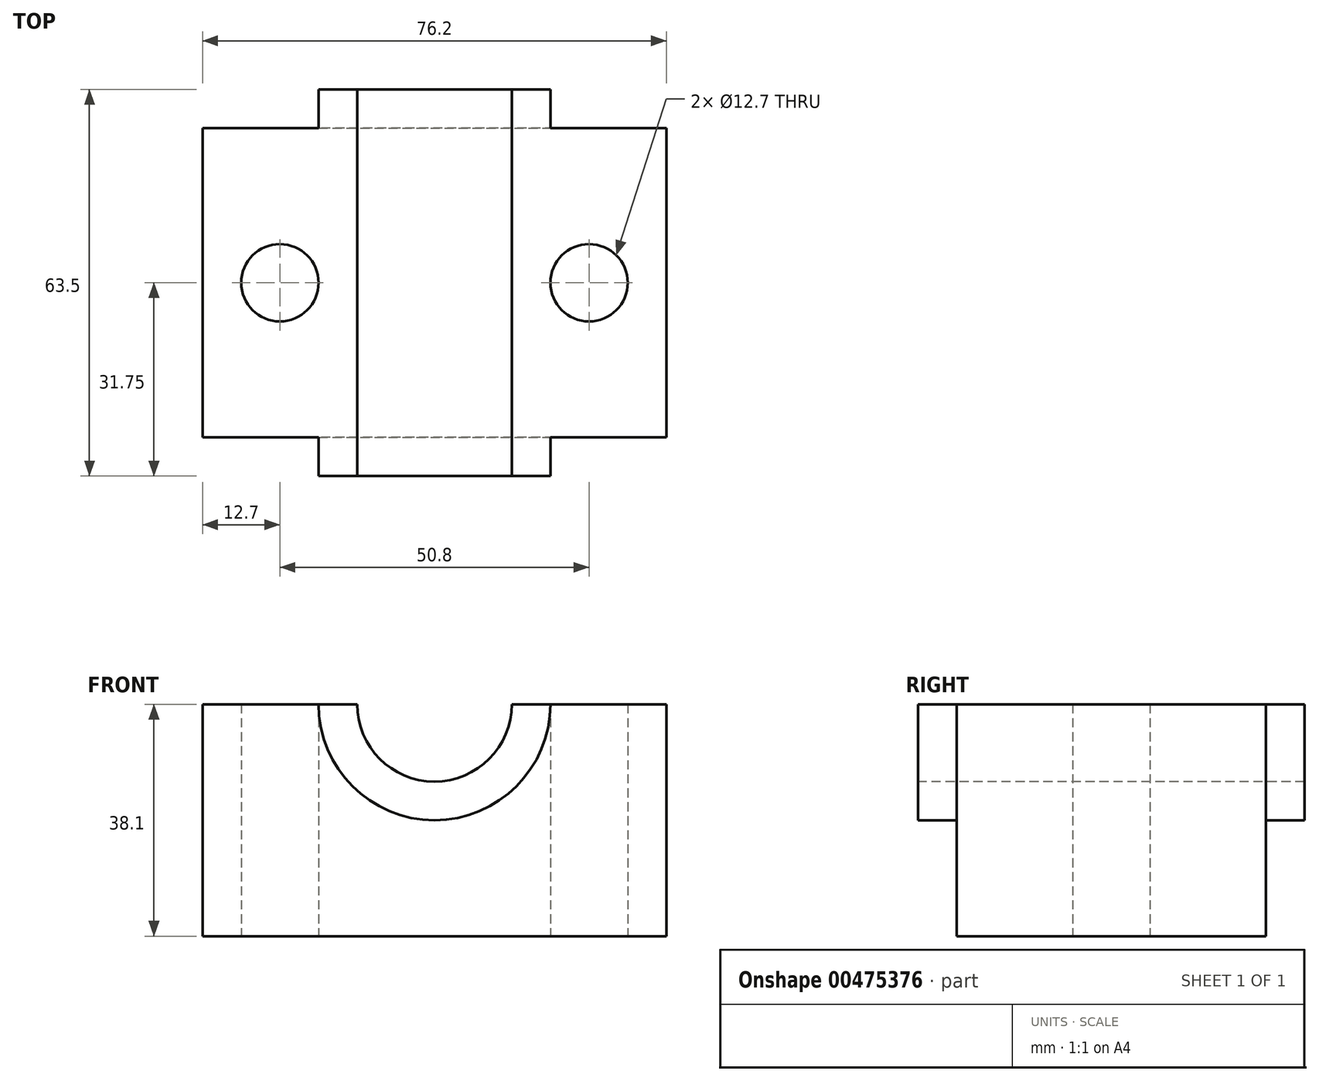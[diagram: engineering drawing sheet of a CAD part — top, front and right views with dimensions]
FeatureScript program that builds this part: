
annotation { "Feature Type Name" : "Feature", "Feature Type Description" : "" }
export const myFeature = defineFeature(function(context is Context, id is Id, definition is map)
    precondition{}
    {
        {
            var Q0;
            Q0=qCreatedBy(makeId("Top.planeOp"),FACE);
            var sketch = newSketch(context, id + "F0", { "sketchPlane" : qUnion([Q0])});
            skLineSegment(sketch, "E0.bottom", {"start": v(38.1, -25.4) * mm, "end": v(-38.1, -25.4) * mm});
            skLineSegment(sketch, "E0.top", {"start": v(38.1, 25.4) * mm, "end": v(-38.1, 25.4) * mm});
            skLineSegment(sketch, "E0.left", {"start": v(38.1, -25.4) * mm, "end": v(38.1, 25.4) * mm});
            skLineSegment(sketch, "E0.right", {"start": v(-38.1, -25.4) * mm, "end": v(-38.1, 25.4) * mm});
            skPoint(sketch, "E0.middle", {"position": v(0, 0) * mm});
            skLineSegment(sketch, "E1", {"start": v(-38.1, 0) * mm, "end": v(-25.4, 0) * mm, "construction": true});
            skPoint(sketch, "E1.endSnap0", {"position": v(-38.1, 0) * mm});
            skLineSegment(sketch, "E2", {"start": v(38.1, 0) * mm, "end": v(25.4, 0) * mm, "construction": true});
            skPoint(sketch, "E2.endSnap0", {"position": v(38.1, 0) * mm});
            skCircle(sketch, "E3", {"center": v(-25.4, 0) * mm, "radius": 6.35 * mm});
            skCircle(sketch, "E4", {"center": v(25.4, 0) * mm, "radius": 6.35 * mm});
            skSolve(sketch);
        }
        {
            var Q0;
            Q0 = qSketchRegion(id + "F0", true);
            extrude(context, id + "F1", {"entities" : qUnion([Q0]), "depth" : 38.1 * mm});
        }
        {
            var Q0;
            Q0=makeQuery(id+"F1.opExtrude","SWEPT_FACE",FACE,{"disambiguationData":[OSD([sQuery(id+"F0.wireOp",EDGE,"E0.bottom")])]});
            var sketch = newSketch(context, id + "F2", { "sketchPlane" : qUnion([Q0])});
            skCircle(sketch, "E5", {"center": v(0, 38.1) * mm, "radius": 19.05 * mm});
            skCircle(sketch, "E6", {"center": v(0, 38.1) * mm, "radius": 12.7 * mm});
            skSolve(sketch);
        }
        {
            var Q0;
            {var subQ0=sQuery(id+"F2.wireOp",EDGE,"E6");var subQ1=makeQuery(id+"F1.opExtrude","CAP_EDGE",EDGE,{"disambiguationData":[OSD([sQuery(id+"F0.wireOp",EDGE,"E0.bottom")])],"isStart":false});var subQ2=makeQuery(id+"F2.imprint","INTERSECT",VERTEX,{"disambiguationData":[OD(0.0)],"derivedFrom":[subQ1,subQ0]});Q0=makeQuery(id+"F2.imprint","IMPRINT",FACE,{"disambiguationData":[TD([[makeQuery(id+"F2.imprint","IMPRINT",EDGE,{"disambiguationData":[TD([[subQ2,1.0]])],"derivedFrom":subQ0}),1.0]])]});}
            extrude(context, id + "F3", {"entities" : qUnion([Q0]), "operationType" : NewBodyOperationType.REMOVE, "endBound" : BoundingType.THROUGH_ALL, "oppositeDirection" : true, "depth" : 25.4 * mm});
        }
        {
            var Q0;
            {var subQ0=sQuery(id+"F2.wireOp",EDGE,"E5");var subQ1=makeQuery(id+"F1.opExtrude","CAP_EDGE",EDGE,{"disambiguationData":[OSD([sQuery(id+"F0.wireOp",EDGE,"E0.bottom")])],"isStart":false});var subQ2=makeQuery(id+"F2.imprint","INTERSECT",VERTEX,{"disambiguationData":[OD(0.0)],"derivedFrom":[subQ1,subQ0]});Q0=makeQuery(id+"F2.imprint","IMPRINT",FACE,{"disambiguationData":[TD([[makeQuery(id+"F2.imprint","IMPRINT",EDGE,{"disambiguationData":[TD([[subQ2,1.0]])],"derivedFrom":subQ0}),1.0]])]});}
            extrude(context, id + "F4", {"entities" : qUnion([Q0]), "operationType" : NewBodyOperationType.ADD, "depth" : 6.35 * mm});
        }
        {
            var Q0;
            Q0=makeQuery(id+"F1.opExtrude","SWEPT_BODY",BODY,{"disambiguationData":[OSD([sQuery(id+"F0.wireOp",EDGE,"E0.bottom"),sQuery(id+"F0.wireOp",EDGE,"E0.top"),sQuery(id+"F0.wireOp",EDGE,"E0.left"),sQuery(id+"F0.wireOp",EDGE,"E0.right"),sQuery(id+"F0.wireOp",EDGE,"E3"),sQuery(id+"F0.wireOp",EDGE,"E4")])]});
            var Q1;
            Q1=qCreatedBy(makeId("Front.planeOp"),FACE);
            mirror(context, id + "F5", {"operationType" : NewBodyOperationType.ADD, "entities" : qUnion([Q0]), "mirrorPlane" : qUnion([Q1])});
        }
    });
